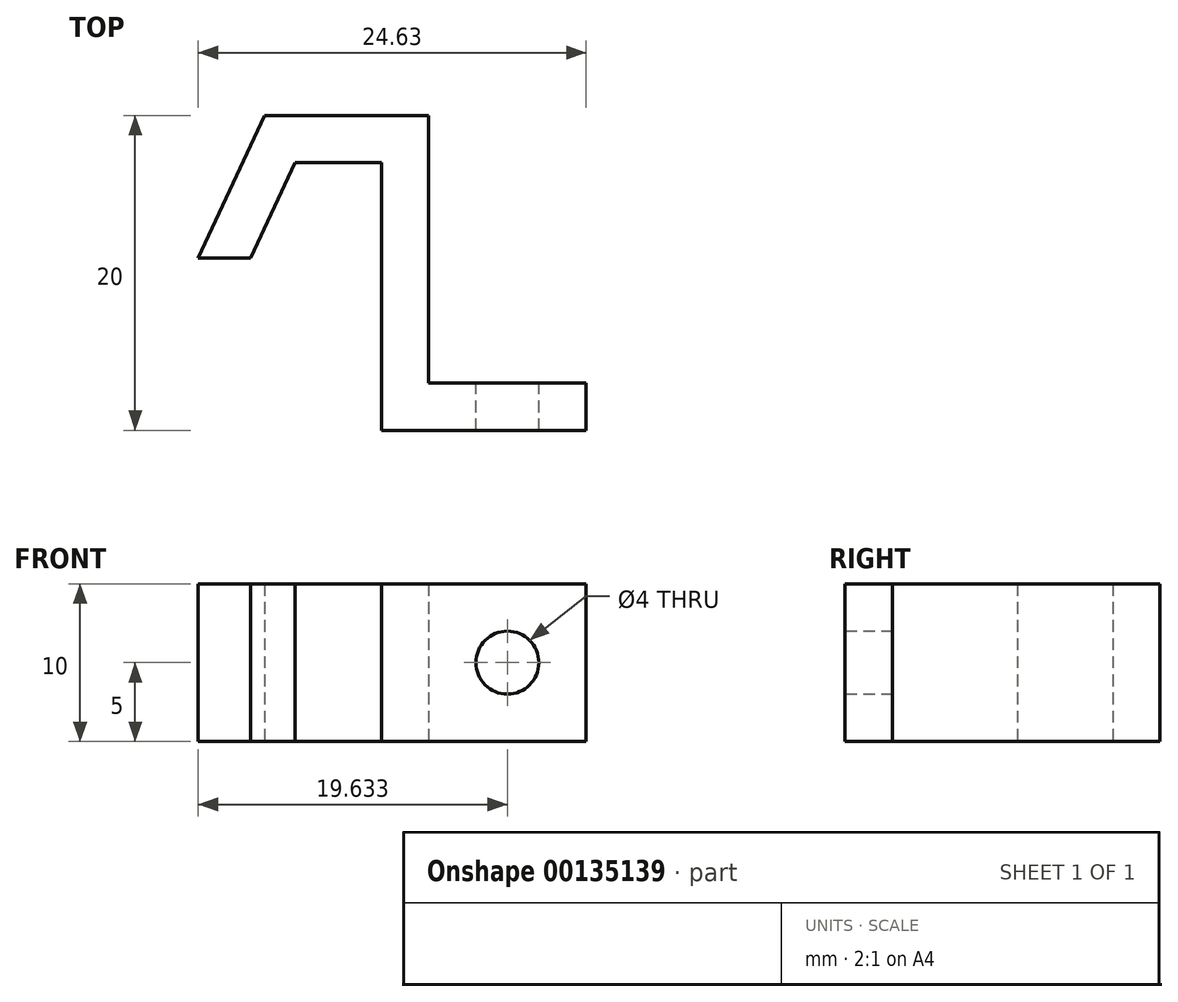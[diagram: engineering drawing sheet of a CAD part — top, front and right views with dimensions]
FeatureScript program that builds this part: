
annotation { "Feature Type Name" : "Feature", "Feature Type Description" : "" }
export const myFeature = defineFeature(function(context is Context, id is Id, definition is map)
    precondition{}
    {
        {
            var Q0;
            Q0=qCreatedBy(makeId("Top.planeOp"),FACE);
            var sketch = newSketch(context, id + "F0", { "sketchPlane" : qUnion([Q0])});
            skLineSegment(sketch, "E0", {"start": v(10.91, -10.94) * mm, "end": v(-2.09, -10.94) * mm});
            skLineSegment(sketch, "E1", {"start": v(-2.09, -10.94) * mm, "end": v(-2.09, 6.06) * mm});
            skLineSegment(sketch, "E2", {"start": v(-2.09, 6.06) * mm, "end": v(-7.59, 6.06) * mm});
            skLineSegment(sketch, "E3", {"start": v(-7.59, 6.06) * mm, "end": v(-10.41, 0) * mm});
            skLineSegment(sketch, "E4", {"start": v(-10.41, 0) * mm, "end": v(-13.72, 0) * mm});
            skLineSegment(sketch, "E5", {"start": v(-13.72, 0) * mm, "end": v(-9.5, 9.06) * mm});
            skLineSegment(sketch, "E6", {"start": v(-9.5, 9.06) * mm, "end": v(0.91, 9.06) * mm});
            skLineSegment(sketch, "E7", {"start": v(0.91, 9.06) * mm, "end": v(0.91, -7.94) * mm});
            skLineSegment(sketch, "E8", {"start": v(0.91, -7.94) * mm, "end": v(10.91, -7.94) * mm});
            skLineSegment(sketch, "E9", {"start": v(10.91, -7.94) * mm, "end": v(10.91, -10.94) * mm});
            skSolve(sketch);
        }
        {
            var Q0;
            Q0=qSketchRegion(id+"F0",true);
            extrude(context, id + "F1", {"entities" : qUnion([Q0]), "depth" : 10 * mm});
        }
        {
            var Q0;
            Q0=makeQuery(id+"F1.opExtrude","SWEPT_FACE",FACE,{"disambiguationData":[OSD([sQuery(id+"F0.wireOp",EDGE,"E8")])]});
            var sketch = newSketch(context, id + "F2", { "sketchPlane" : qUnion([Q0])});
            skPoint(sketch, "E10", {"position": v(-5.91, 5) * mm});
            skSolve(sketch);
        }
        {
            var Q0;
            Q0=sQuery(id+"F2.wireOp",VERTEX,"E10");
            var Q1;
            Q1=makeQuery(id+"F1.opExtrude","SWEPT_BODY",BODY,{"disambiguationData":[OSD([sQuery(id+"F0.wireOp",EDGE,"E0"),sQuery(id+"F0.wireOp",EDGE,"E1"),sQuery(id+"F0.wireOp",EDGE,"E2"),sQuery(id+"F0.wireOp",EDGE,"E3"),sQuery(id+"F0.wireOp",EDGE,"E4"),sQuery(id+"F0.wireOp",EDGE,"E5"),sQuery(id+"F0.wireOp",EDGE,"E6"),sQuery(id+"F0.wireOp",EDGE,"E7"),sQuery(id+"F0.wireOp",EDGE,"E8"),sQuery(id+"F0.wireOp",EDGE,"E9")])]});
            hole(context, id + "F3", {"style" : HoleStyle.SIMPLE, "endStyle" : HoleEndStyle.THROUGH, "holeDiameter" : 4 * mm, "locations" : qUnion([Q0]), "scope" : qUnion([Q1]), "isTappedThrough" : true});
        }
    });
